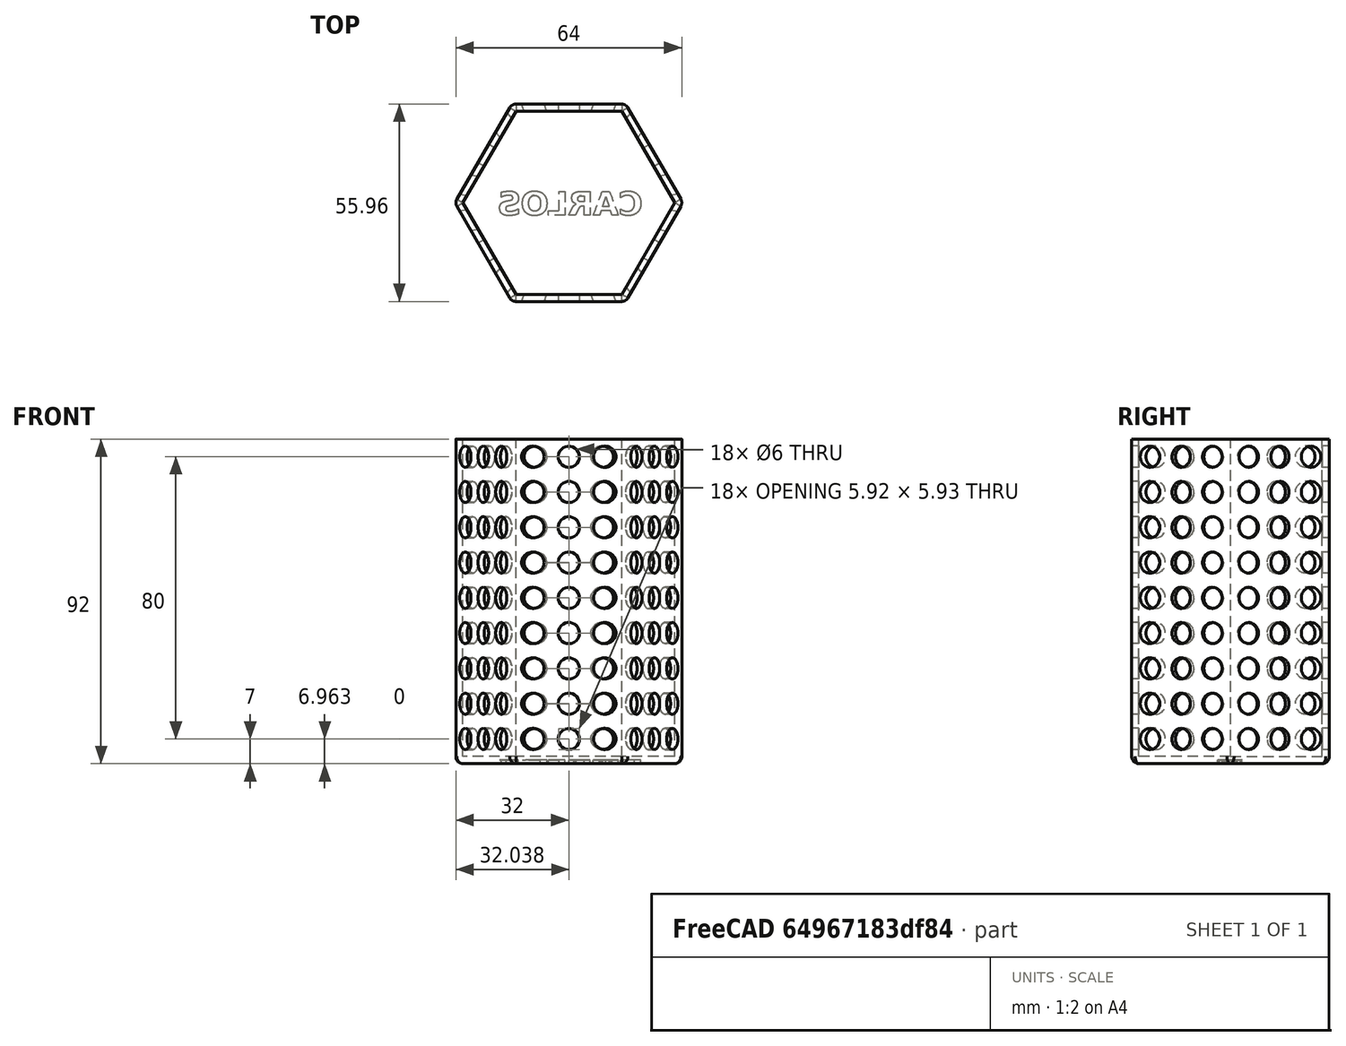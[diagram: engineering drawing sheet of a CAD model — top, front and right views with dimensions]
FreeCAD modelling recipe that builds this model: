
FCSTD DOCUMENT  (FreeCAD 0.14R3702 (Git))
Label: cubilete_bolis
License: CC-BY 3.0
LicenseURL: http://creativecommons.org/licenses/by/3.0/
objects: Part::Feature×9, Part::Extrusion×9, Part::Cut×5, Part::FeaturePython×2, Part::Prism×1, App::MeasureDistance×1, Part::Thickness×1, Part::Cylinder×1, Part::MultiFuse×1
note: 29 computed .brp shape members not serialized (recipe doc carries the construction recipe); baked Part::Feature solids carry a one-line shape summary decoded from their .brp

FEATURE [Part::Prism] Prism  label="Prisma"
  Circumradius = 30
  Height = 90
  Polygon = 6
FEATURE [App::MeasureDistance] Distance  label="Distance: 60.000"
  Distance = 60
  P1 = (30,0,0)
  P2 = (-30,0,0)
FEATURE [Part::Thickness] Thickness
  Faces = -> Prism [Face8]
  Intersection = false
  Join = 0
  Mode = 0
  SelfIntersection = false
  Value = 2
FEATURE [Part::Cylinder] Cylinder  label="Cilindro"
  Angle = 360
  Height = 80
  Placement = pos=(-34.641,-20,5) rot=(-0.250563,0.935113,0.250563;1.63783rad)
  Radius = 3
FEATURE [Part::FeaturePython] Array  # Draft array (typed FeaturePython)
  Angle = 360
  ArrayType = 0
  Axis = (0,0,1)
  Base = -> Cylinder
  Center = (0,0,0)
  IntervalX = (1,0,0)
  IntervalY = (0,1,0)
  IntervalZ = (0,0,10)
  NumberPolar = 1
  NumberX = 1
  NumberY = 1
  NumberZ = 20
FEATURE [Part::FeaturePython] Array001  # Draft array (typed FeaturePython)
  Angle = 360
  ArrayType = 1
  Axis = (0,0,1)
  Base = -> Array
  Center = (0,0,0)
  IntervalX = (1,0,0)
  IntervalY = (0,1,0)
  IntervalZ = (0,0,1)
  NumberPolar = 9
  NumberX = 1
  NumberY = 1
  NumberZ = 1
FEATURE [Part::Cut] Cut  label="PortaBolis"
  Base = -> Thickness
  Tool = -> Array001
FEATURE [Part::Feature] path2998
  shape: bbox 5.734 x 6.994 x 2e-07 mm, 0 faces, 0 solids (baked)
FEATURE [Part::Feature] path3000
  shape: bbox 7.066 x 6.741 x 2e-07 mm, 0 faces, 0 solids (baked)
FEATURE [Part::Feature] path3000001
  shape: bbox 1.847 x 2.682 x 2e-07 mm, 0 faces, 0 solids (baked)
FEATURE [Part::Feature] path3002
  shape: bbox 1.752 x 1.729 x 2e-07 mm, 0 faces, 0 solids (baked)
FEATURE [Part::Feature] path3002001
  shape: bbox 6.086 x 6.741 x 2e-07 mm, 0 faces, 0 solids (baked)
FEATURE [Part::Feature] path3004
  shape: bbox 4.791 x 6.741 x 2e-07 mm, 0 faces, 0 solids (baked)
FEATURE [Part::Feature] path3006
  shape: bbox 3.346 x 4.475 x 2e-07 mm, 0 faces, 0 solids (baked)
FEATURE [Part::Feature] path3006001
  shape: bbox 6.935 x 6.994 x 2e-07 mm, 0 faces, 0 solids (baked)
FEATURE [Part::Feature] path3008
  shape: bbox 5.319 x 6.994 x 2e-07 mm, 0 faces, 0 solids (baked)
FEATURE [Part::Extrusion] Extrude
  Base = -> path2998
  Dir = (0,0,-2)
  Solid = true
FEATURE [Part::Extrusion] Extrude001
  Base = -> path3000
  Dir = (0,0,-2)
  Solid = true
FEATURE [Part::Extrusion] Extrude002
  Base = -> path3000001
  Dir = (0,0,-2)
  Solid = true
FEATURE [Part::Extrusion] Extrude003
  Base = -> path3002
  Dir = (0,0,-2)
  Solid = true
FEATURE [Part::Extrusion] Extrude004
  Base = -> path3002001
  Dir = (0,0,-2)
  Solid = true
FEATURE [Part::Extrusion] Extrude005
  Base = -> path3004
  Dir = (0,0,-2)
  Solid = true
FEATURE [Part::Extrusion] Extrude006
  Base = -> path3006
  Dir = (0,0,-2)
  Solid = true
FEATURE [Part::Extrusion] Extrude007
  Base = -> path3006001
  Dir = (0,0,-2)
  Solid = true
FEATURE [Part::Extrusion] Extrude008
  Base = -> path3008
  Dir = (0,0,-2)
  Solid = true
FEATURE [Part::Cut] Cut001
  Base = -> Extrude001
  Tool = -> Extrude002
FEATURE [Part::Cut] Cut002
  Base = -> Extrude004
  Tool = -> Extrude003
FEATURE [Part::Cut] Cut003
  Base = -> Extrude007
  Tool = -> Extrude006
FEATURE [Part::MultiFuse] Fusion  label="CARLOS"
  Placement = pos=(0,0,-3) rot=(0,1,0;3.14159rad)
  Shapes = -> [Extrude,Extrude005,Cut002,Cut003,Cut001,Extrude008]
FEATURE [Part::Cut] Cut004
  Base = -> Cut
  Tool = -> Fusion
